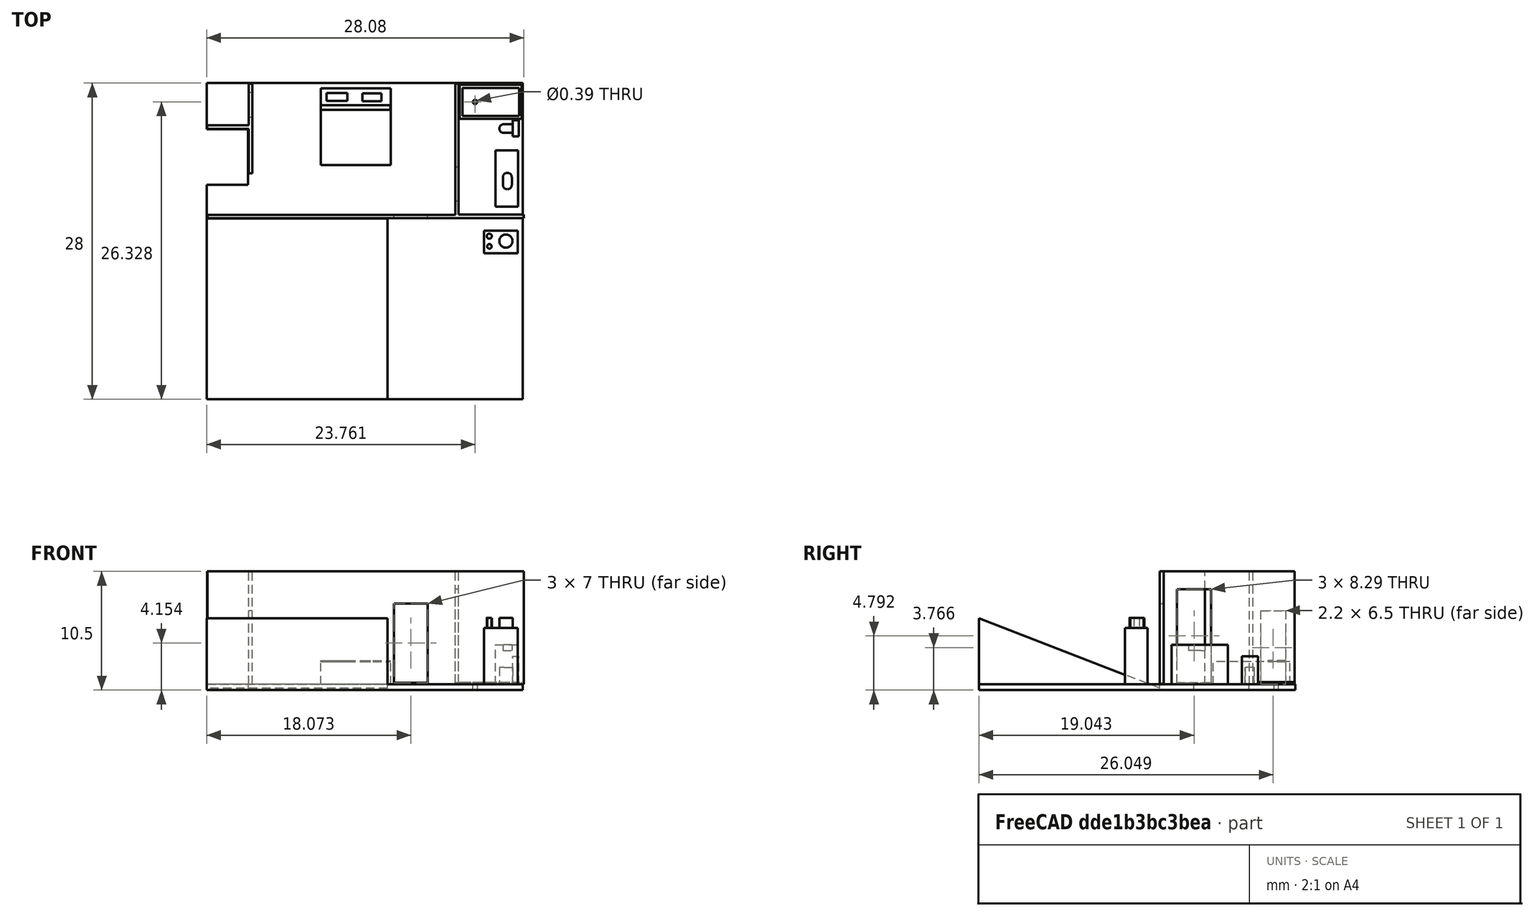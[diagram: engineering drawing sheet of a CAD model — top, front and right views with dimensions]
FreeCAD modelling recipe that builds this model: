
FCSTD DOCUMENT  (FreeCAD 0.19R)
Label: Addtion2ndStoryC
License: All rights reserved
LicenseURL: http://en.wikipedia.org/wiki/All_rights_reserved
objects: Sketcher::SketchObject×18, PartDesign::Pad×11, PartDesign::Pocket×7, PartDesign::Body×1, Mesh::Feature×1
note: 55 computed .brp shape members not serialized (recipe doc carries the construction recipe); baked Part::Feature solids carry a one-line shape summary decoded from their .brp

FEATURE [Sketcher::SketchObject] Sketch
  FullyConstrained = true
  MapMode = 5
  Support = -> [XY_Plane]
  sketch-geometry (6):
    g0: LineSegment StartX=-16 StartY=12 StartZ=0 EndX=12 EndY=12 EndZ=0
    g1: LineSegment StartX=0 StartY=0 StartZ=0 EndX=-16 EndY=0 EndZ=0
    g2: LineSegment StartX=-16 StartY=0 StartZ=0 EndX=-16 EndY=12 EndZ=0
    g3: LineSegment StartX=12 StartY=12 StartZ=0 EndX=12 EndY=-16 EndZ=0
    g4: LineSegment StartX=12 StartY=-16 StartZ=0 EndX=0 EndY=-16 EndZ=0
    g5: LineSegment StartX=0 StartY=-16 StartZ=0 EndX=0 EndY=0 EndZ=0
  constraints (17):
    c: Coincident(g1,g2)
    c: Coincident(g2,g0)
    c: Horizontal(g0)
    c: Horizontal(g1)
    c: Vertical(g2)
    c: DistanceX(g0) = 12
    c: DistanceX(g0) = -16
    c: DistanceY(g0) = 12
    c: Coincident(g1,g-1)
    c: Coincident(g0,g3)
    c: Coincident(g3,g4)
    c: PointOnObject(g4,g-2)
    c: Coincident(g4,g5)
    c: Coincident(g5,g1)
    c: Vertical(g3)
    c: Horizontal(g4)
    c: Distance(g5) = 16
FEATURE [PartDesign::Pad] Pad
  Direction = (1,1,1)
  Length = 0.5
  Length2 = 100
  Profile = -> Sketch
  Type = 0
FEATURE [Sketcher::SketchObject] Sketch001
  FullyConstrained = false
  MapMode = 5
  Placement = pos=(0,0,0.5) rot=(0,0,1;0rad)
  Support = -> [Pad]
  sketch-geometry (17):
    g0: LineSegment StartX=-15.9532 StartY=7.94663 StartZ=0 EndX=-15.9532 EndY=8.27663 EndZ=0
    g1: LineSegment StartX=-12.2832 StartY=11.9466 StartZ=0 EndX=-11.9532 EndY=11.9466 EndZ=0
    g2: LineSegment StartX=-11.9532 StartY=11.9466 StartZ=0 EndX=-11.9532 EndY=7.94663 EndZ=0
    g3: LineSegment StartX=12.0789 StartY=0.353614 StartZ=0 EndX=12.0789 EndY=0.023614 EndZ=0
    g4: LineSegment StartX=12.0789 StartY=0.023614 StartZ=0 EndX=-15.9253 EndY=0.023614 EndZ=0
    g5: LineSegment StartX=-15.9253 StartY=0.023614 StartZ=0 EndX=-15.9253 EndY=0.33 EndZ=0
    g6: LineSegment StartX=6.3 StartY=11.9503 StartZ=0 EndX=6 EndY=11.9503 EndZ=0
    g7: LineSegment StartX=6 StartY=11.9503 StartZ=0 EndX=6 EndY=0.33 EndZ=0
    g8: LineSegment StartX=6.3 StartY=0.353614 StartZ=0 EndX=6.3 EndY=11.9503 EndZ=0
    g9: LineSegment StartX=-15.9253 StartY=0.33 StartZ=0 EndX=6 EndY=0.33 EndZ=0
    g10: LineSegment StartX=6.3 StartY=0.353614 StartZ=0 EndX=12.0789 EndY=0.353614 EndZ=0
    g11: LineSegment StartX=-15.9532 StartY=8.27663 StartZ=0 EndX=-12.2832 EndY=8.27663 EndZ=0
    g12: LineSegment StartX=-12.2832 StartY=11.9466 StartZ=0 EndX=-12.2832 EndY=8.27663 EndZ=0
    g13: LineSegment StartX=-15.9532 StartY=7.94663 StartZ=0 EndX=-12.2832 EndY=7.94663 EndZ=0
    g14: LineSegment StartX=-12.2832 StartY=7.94663 StartZ=0 EndX=-12.2832 EndY=4 EndZ=0
    g15: LineSegment StartX=-12.2832 StartY=4 StartZ=0 EndX=-11.9532 EndY=4 EndZ=0
    g16: LineSegment StartX=-11.9532 StartY=7.94663 StartZ=0 EndX=-11.9532 EndY=4 EndZ=0
  constraints (40):
    c: Vertical(g0)
    c: Coincident(g1,g2)
    c: Horizontal(g1)
    c: Vertical(g2)
    c: Distance(g1) = 0.33
    c: Distance(g0) = 0.33
    c: Distance(g2) = 4
    c: Coincident(g3,g4)
    c: Coincident(g4,g5)
    c: Horizontal(g4)
    c: Vertical(g3)
    c: Vertical(g5)
    c: Distance(g3) = 0.33
    c: Coincident(g6,g7)
    c: Coincident(g8,g6)
    c: Horizontal(g6)
    c: Vertical(g7)
    c: Vertical(g8)
    c: Distance(g6) = 0.3
    c: DistanceX(g6) = 6
    c: Coincident(g9,g5)
    c: Coincident(g9,g7)
    c: Horizontal(g9)
    c: Coincident(g10,g8)
    c: Coincident(g10,g3)
    c: Horizontal(g10)
    c: Coincident(g11,g0)
    c: Horizontal(g11)
    c: Coincident(g12,g1)
    c: Coincident(g12,g11)
    c: Vertical(g12)
    c: Coincident(g13,g0)
    c: Horizontal(g13)
    c: Vertical(g14)
    c: Coincident(g15,g14)
    c: Coincident(g16,g15)
    c: Vertical(g16)
    c: DistanceY(g15) = 4
    c: Horizontal(g15)
    c: DistanceY(g7) = 0.33
FEATURE [PartDesign::Pad] Pad001
  BaseFeature = -> Pad
  Direction = (1,1,1)
  Length = 10
  Length2 = 100
  Profile = -> Sketch001
  Type = 0
FEATURE [Sketcher::SketchObject] Sketch002
  FullyConstrained = false
  MapMode = 5
  Placement = pos=(0,0,0.5) rot=(0,0,1;0rad)
  Support = -> [Pad001]
  sketch-geometry (4):
    g0: LineSegment StartX=-16.4037 StartY=7.90912 StartZ=0 EndX=-12.3288 EndY=7.90912 EndZ=0
    g1: LineSegment StartX=-12.3288 StartY=7.90912 StartZ=0 EndX=-12.3288 EndY=3 EndZ=0
    g2: LineSegment StartX=-12.3288 StartY=3 StartZ=0 EndX=-16.4037 EndY=3 EndZ=0
    g3: LineSegment StartX=-16.4037 StartY=3 StartZ=0 EndX=-16.4037 EndY=7.90912 EndZ=0
  constraints (9):
    c: Coincident(g0,g1)
    c: Coincident(g1,g2)
    c: Coincident(g2,g3)
    c: Coincident(g3,g0)
    c: Horizontal(g0)
    c: Horizontal(g2)
    c: Vertical(g1)
    c: Vertical(g3)
    c: DistanceY(g1) = 3
FEATURE [PartDesign::Pocket] Pocket
  BaseFeature = -> Pad001
  Length = 5
  Length2 = 100
  Profile = -> Sketch002
  Type = 0
FEATURE [Sketcher::SketchObject] Sketch003
  FullyConstrained = false
  MapMode = 5
  Placement = pos=(6.3,0,0) rot=(0.57735,0.57735,0.57735;2.0944rad)
  Support = -> [Pocket]
  sketch-geometry (4):
    g0: LineSegment StartX=1.54342 StartY=8.93566 StartZ=0 EndX=4.54342 EndY=8.93566 EndZ=0
    g1: LineSegment StartX=4.54342 StartY=8.93566 StartZ=0 EndX=4.54342 EndY=0.648454 EndZ=0
    g2: LineSegment StartX=4.54342 StartY=0.648454 StartZ=0 EndX=1.54342 EndY=0.648454 EndZ=0
    g3: LineSegment StartX=1.54342 StartY=0.648454 StartZ=0 EndX=1.54342 EndY=8.93566 EndZ=0
  constraints (9):
    c: Coincident(g0,g1)
    c: Coincident(g1,g2)
    c: Coincident(g2,g3)
    c: Coincident(g3,g0)
    c: Horizontal(g0)
    c: Horizontal(g2)
    c: Vertical(g1)
    c: Vertical(g3)
    c: Distance(g0) = 3
FEATURE [PartDesign::Pocket] Pocket001
  BaseFeature = -> Pocket
  Length = 5
  Length2 = 100
  Profile = -> Sketch003
  Type = 0
FEATURE [Sketcher::SketchObject] Sketch004
  FullyConstrained = false
  MapMode = 5
  Placement = pos=(0,0.023614,0) rot=(1,0,0;1.5708rad)
  Support = -> [Pocket001]
  sketch-geometry (4):
    g0: LineSegment StartX=0.573152 StartY=7.65396 StartZ=0 EndX=3.57315 EndY=7.65396 EndZ=0
    g1: LineSegment StartX=3.57315 StartY=7.65396 StartZ=0 EndX=3.57315 EndY=0.653959 EndZ=0
    g2: LineSegment StartX=3.57315 StartY=0.653959 StartZ=0 EndX=0.573152 EndY=0.653959 EndZ=0
    g3: LineSegment StartX=0.573152 StartY=0.653959 StartZ=0 EndX=0.573152 EndY=7.65396 EndZ=0
  constraints (10):
    c: Coincident(g0,g1)
    c: Coincident(g1,g2)
    c: Coincident(g2,g3)
    c: Coincident(g3,g0)
    c: Horizontal(g0)
    c: Horizontal(g2)
    c: Vertical(g1)
    c: Vertical(g3)
    c: Distance(g0) = 3
    c: Distance(g1) = 7
FEATURE [PartDesign::Pocket] Pocket002
  BaseFeature = -> Pocket001
  Length = 5
  Length2 = 100
  Profile = -> Sketch004
  Type = 0
FEATURE [Sketcher::SketchObject] Sketch005
  FullyConstrained = false
  MapMode = 5
  Placement = pos=(-11.9532,0,0) rot=(0.57735,0.57735,0.57735;2.0944rad)
  Support = -> [Pocket002]
  sketch-geometry (4):
    g0: LineSegment StartX=8.94938 StartY=7.01579 StartZ=0 EndX=11.1494 EndY=7.01579 EndZ=0
    g1: LineSegment StartX=11.1494 StartY=7.01579 StartZ=0 EndX=11.1494 EndY=0.51579 EndZ=0
    g2: LineSegment StartX=11.1494 StartY=0.51579 StartZ=0 EndX=8.94938 EndY=0.51579 EndZ=0
    g3: LineSegment StartX=8.94938 StartY=0.51579 StartZ=0 EndX=8.94938 EndY=7.01579 EndZ=0
  constraints (10):
    c: Coincident(g0,g1)
    c: Coincident(g1,g2)
    c: Coincident(g2,g3)
    c: Coincident(g3,g0)
    c: Horizontal(g0)
    c: Horizontal(g2)
    c: Vertical(g1)
    c: Vertical(g3)
    c: Distance(g0) = 2.2
    c: Distance(g1) = 6.5
FEATURE [PartDesign::Pocket] Pocket003
  BaseFeature = -> Pocket002
  Length = 5
  Length2 = 100
  Profile = -> Sketch005
  Type = 0
FEATURE [Sketcher::SketchObject] Sketch006
  FullyConstrained = false
  MapMode = 5
  Placement = pos=(0,0,0.5) rot=(0,0,1;0rad)
  Support = -> [Pocket003]
  sketch-geometry (4):
    g0: LineSegment StartX=6.38983 StartY=11.8429 StartZ=0 EndX=11.8898 EndY=11.8429 EndZ=0
    g1: LineSegment StartX=11.8898 StartY=11.8429 StartZ=0 EndX=11.8898 EndY=8.84289 EndZ=0
    g2: LineSegment StartX=11.8898 StartY=8.84289 StartZ=0 EndX=6.38983 EndY=8.84289 EndZ=0
    g3: LineSegment StartX=6.38983 StartY=8.84289 StartZ=0 EndX=6.38983 EndY=11.8429 EndZ=0
  constraints (10):
    c: Coincident(g0,g1)
    c: Coincident(g1,g2)
    c: Coincident(g2,g3)
    c: Coincident(g3,g0)
    c: Horizontal(g0)
    c: Horizontal(g2)
    c: Vertical(g1)
    c: Vertical(g3)
    c: Distance(g2) = 5.5
    c: Distance(g1) = 3
FEATURE [PartDesign::Pad] Pad002
  BaseFeature = -> Pocket003
  Direction = (1,1,1)
  Length = 0.2
  Length2 = 100
  Profile = -> Sketch006
  Type = 0
FEATURE [Sketcher::SketchObject] Sketch007
  FullyConstrained = false
  MapMode = 5
  Placement = pos=(0,0,0.7) rot=(0,0,1;0rad)
  Support = -> [Pad002]
  sketch-geometry (4):
    g0: LineSegment StartX=6.64692 StartY=11.5659 StartZ=0 EndX=11.6693 EndY=11.5659 EndZ=0
    g1: LineSegment StartX=11.6693 StartY=11.5659 StartZ=0 EndX=11.6693 EndY=9.09872 EndZ=0
    g2: LineSegment StartX=11.6693 StartY=9.09872 StartZ=0 EndX=6.64692 EndY=9.09872 EndZ=0
    g3: LineSegment StartX=6.64692 StartY=9.09872 StartZ=0 EndX=6.64692 EndY=11.5659 EndZ=0
  constraints (8):
    c: Coincident(g0,g1)
    c: Coincident(g1,g2)
    c: Coincident(g2,g3)
    c: Coincident(g3,g0)
    c: Horizontal(g0)
    c: Horizontal(g2)
    c: Vertical(g1)
    c: Vertical(g3)
FEATURE [PartDesign::Pocket] Pocket004
  BaseFeature = -> Pad002
  Length = 0.2
  Length2 = 100
  Profile = -> Sketch007
  Type = 0
FEATURE [Sketcher::SketchObject] Sketch008
  FullyConstrained = false
  MapMode = 5
  Placement = pos=(0,0,0.5) rot=(0,0,1;0rad)
  Support = -> [Pocket004]
  sketch-geometry (4):
    g0: ArcOfCircle CenterX=10.2998 CenterY=7.96616 CenterZ=0 NormalX=0 NormalY=0 NormalZ=1 AngleXU=0 Radius=0.384687 StartAngle=1.5708 EndAngle=4.71239
    g1: ArcOfCircle CenterX=11.0789 CenterY=7.96616 CenterZ=0 NormalX=0 NormalY=0 NormalZ=1 AngleXU=0 Radius=0.384687 StartAngle=4.71239 EndAngle=7.85398
    g2: LineSegment StartX=10.2998 StartY=7.58147 StartZ=0 EndX=11.0789 EndY=7.58147 EndZ=0
    g3: LineSegment StartX=10.2998 StartY=8.35084 StartZ=0 EndX=11.0789 EndY=8.35084 EndZ=0
  constraints (6):
    c: Tangent(g0,g3) = 1.5708
    c: Tangent(g0,g2) = -1.5708
    c: Tangent(g2,g1) = -1.5708
    c: Tangent(g3,g1) = 1.5708
    c: Horizontal(g2)
    c: Equal(g0,g1)
FEATURE [PartDesign::Pad] Pad003
  BaseFeature = -> Pocket004
  Direction = (1,1,1)
  Length = 1.5
  Length2 = 100
  Profile = -> Sketch008
  Type = 0
FEATURE [Sketcher::SketchObject] Sketch009
  FullyConstrained = false
  MapMode = 5
  Placement = pos=(0,0,0.5) rot=(0,0,1;0rad)
  Support = -> [Pad003]
  sketch-geometry (4):
    g0: LineSegment StartX=11.1017 StartY=8.69932 StartZ=0 EndX=11.648 EndY=8.69932 EndZ=0
    g1: LineSegment StartX=11.648 StartY=8.69932 StartZ=0 EndX=11.648 EndY=7.2719 EndZ=0
    g2: LineSegment StartX=11.648 StartY=7.2719 StartZ=0 EndX=11.1017 EndY=7.2719 EndZ=0
    g3: LineSegment StartX=11.1017 StartY=7.2719 StartZ=0 EndX=11.1017 EndY=8.69932 EndZ=0
  constraints (8):
    c: Coincident(g0,g1)
    c: Coincident(g1,g2)
    c: Coincident(g2,g3)
    c: Coincident(g3,g0)
    c: Horizontal(g0)
    c: Horizontal(g2)
    c: Vertical(g1)
    c: Vertical(g3)
FEATURE [PartDesign::Pad] Pad004
  BaseFeature = -> Pad003
  Direction = (1,1,1)
  Length = 2.5
  Length2 = 100
  Profile = -> Sketch009
  Type = 0
FEATURE [Sketcher::SketchObject] Sketch010
  FullyConstrained = false
  MapMode = 5
  Placement = pos=(0,0,0.5) rot=(0,0,1;0rad)
  Support = -> [Pad004]
  sketch-geometry (4):
    g0: LineSegment StartX=9.57943 StartY=6.04354 StartZ=0 EndX=11.5794 EndY=6.04354 EndZ=0
    g1: LineSegment StartX=11.5794 StartY=6.04354 StartZ=0 EndX=11.5794 EndY=1.04354 EndZ=0
    g2: LineSegment StartX=11.5794 StartY=1.04354 StartZ=0 EndX=9.57943 EndY=1.04354 EndZ=0
    g3: LineSegment StartX=9.57943 StartY=1.04354 StartZ=0 EndX=9.57943 EndY=6.04354 EndZ=0
  constraints (10):
    c: Coincident(g0,g1)
    c: Coincident(g1,g2)
    c: Coincident(g2,g3)
    c: Coincident(g3,g0)
    c: Horizontal(g0)
    c: Horizontal(g2)
    c: Vertical(g1)
    c: Vertical(g3)
    c: Distance(g3) = 5
    c: Distance(g0) = 2
FEATURE [PartDesign::Pad] Pad005
  BaseFeature = -> Pad004
  Direction = (1,1,1)
  Length = 3.5
  Length2 = 100
  Profile = -> Sketch010
  Type = 0
FEATURE [Sketcher::SketchObject] Sketch011
  FullyConstrained = false
  MapMode = 5
  Placement = pos=(0,0,4) rot=(0,0,1;0rad)
  Support = -> [Pad005]
  sketch-geometry (4):
    g0: ArcOfCircle CenterX=10.6211 CenterY=3.65295 CenterZ=0 NormalX=0 NormalY=0 NormalZ=1 AngleXU=0 Radius=0.396821 StartAngle=4e-16 EndAngle=3.14159
    g1: ArcOfCircle CenterX=10.6211 CenterY=2.98754 CenterZ=0 NormalX=0 NormalY=0 NormalZ=1 AngleXU=0 Radius=0.396821 StartAngle=3.14159 EndAngle=6.28319
    g2: LineSegment StartX=10.2243 StartY=3.65295 StartZ=0 EndX=10.2243 EndY=2.98754 EndZ=0
    g3: LineSegment StartX=11.0179 StartY=3.65295 StartZ=0 EndX=11.0179 EndY=2.98754 EndZ=0
  constraints (6):
    c: Tangent(g0,g3) = 1.5708
    c: Tangent(g0,g2) = -1.5708
    c: Tangent(g2,g1) = -1.5708
    c: Tangent(g3,g1) = 1.5708
    c: Vertical(g2)
    c: Equal(g0,g1)
FEATURE [PartDesign::Pocket] Pocket005
  BaseFeature = -> Pad005
  Length = 0.5
  Length2 = 100
  Profile = -> Sketch011
  Type = 0
FEATURE [Sketcher::SketchObject] Sketch012
  FullyConstrained = false
  MapMode = 5
  Placement = pos=(0,0,0.5) rot=(0,0,1;0rad)
  Support = -> [Pocket005]
  sketch-geometry (4):
    g0: LineSegment StartX=8.54799 StartY=-1.06451 StartZ=0 EndX=11.548 EndY=-1.06451 EndZ=0
    g1: LineSegment StartX=11.548 StartY=-1.06451 StartZ=0 EndX=11.548 EndY=-3.06451 EndZ=0
    g2: LineSegment StartX=11.548 StartY=-3.06451 StartZ=0 EndX=8.54799 EndY=-3.06451 EndZ=0
    g3: LineSegment StartX=8.54799 StartY=-3.06451 StartZ=0 EndX=8.54799 EndY=-1.06451 EndZ=0
  constraints (10):
    c: Coincident(g0,g1)
    c: Coincident(g1,g2)
    c: Coincident(g2,g3)
    c: Coincident(g3,g0)
    c: Horizontal(g0)
    c: Horizontal(g2)
    c: Vertical(g1)
    c: Vertical(g3)
    c: Distance(g0) = 3
    c: Distance(g3) = 2
FEATURE [PartDesign::Pad] Pad006
  BaseFeature = -> Pocket005
  Direction = (1,1,1)
  Length = 5
  Length2 = 100
  Profile = -> Sketch012
  Type = 0
FEATURE [Sketcher::SketchObject] Sketch013
  FullyConstrained = false
  MapMode = 5
  Placement = pos=(0,0,5.5) rot=(0,0,1;0rad)
  Support = -> [Pad006]
  sketch-geometry (3):
    g0: Circle CenterX=10.4922 CenterY=-1.99827 CenterZ=0 NormalX=0 NormalY=0 NormalZ=1 AngleXU=0 Radius=0.586594
    g1: Circle CenterX=9.02211 CenterY=-1.56306 CenterZ=0 NormalX=0 NormalY=0 NormalZ=1 AngleXU=0 Radius=0.221942
    g2: Circle CenterX=9.03178 CenterY=-2.46251 CenterZ=0 NormalX=0 NormalY=0 NormalZ=1 AngleXU=0 Radius=0.200927
FEATURE [PartDesign::Pad] Pad007
  BaseFeature = -> Pad006
  Direction = (1,1,1)
  Length = 0.9
  Length2 = 100
  Profile = -> Sketch013
  Type = 0
FEATURE [Sketcher::SketchObject] Sketch014
  FullyConstrained = false
  MapMode = 5
  Placement = pos=(0,0,0) rot=(0.57735,-0.57735,-0.57735;2.0944rad)
  Support = -> [Pad007]
  sketch-geometry (3):
    g0: LineSegment StartX=-0.434067 StartY=0 StartZ=0 EndX=16 EndY=6.36 EndZ=0
    g1: LineSegment StartX=16 StartY=6.36 StartZ=0 EndX=16 EndY=0 EndZ=0
    g2: LineSegment StartX=16 StartY=0 StartZ=0 EndX=-0.434067 EndY=0 EndZ=0
  constraints (8):
    c: PointOnObject(g0,g-1)
    c: Coincident(g0,g1)
    c: PointOnObject(g1,g-1)
    c: Vertical(g1)
    c: Coincident(g1,g2)
    c: Coincident(g2,g0)
    c: DistanceX(g1) = 16
    c: DistanceY(g1,g1) = 6.36
FEATURE [PartDesign::Pad] Pad008
  BaseFeature = -> Pad007
  Direction = (1,1,1)
  Length = 16
  Length2 = 100
  Profile = -> Sketch014
  Type = 0
FEATURE [Sketcher::SketchObject] Sketch015
  FullyConstrained = false
  MapMode = 5
  Placement = pos=(0,0,0.5) rot=(0,0,1;0rad)
  Support = -> [Pad008]
  sketch-geometry (4):
    g0: LineSegment StartX=-5.89716 StartY=11.5438 StartZ=0 EndX=0.302838 EndY=11.5438 EndZ=0
    g1: LineSegment StartX=0.302838 StartY=11.5438 StartZ=0 EndX=0.302838 EndY=4.74384 EndZ=0
    g2: LineSegment StartX=0.302838 StartY=4.74384 StartZ=0 EndX=-5.89716 EndY=4.74384 EndZ=0
    g3: LineSegment StartX=-5.89716 StartY=4.74384 StartZ=0 EndX=-5.89716 EndY=11.5438 EndZ=0
  constraints (10):
    c: Coincident(g0,g1)
    c: Coincident(g1,g2)
    c: Coincident(g2,g3)
    c: Coincident(g3,g0)
    c: Horizontal(g0)
    c: Horizontal(g2)
    c: Vertical(g1)
    c: Vertical(g3)
    c: Distance(g3) = 6.8
    c: Distance(g0) = 6.2
FEATURE [PartDesign::Pad] Pad009
  BaseFeature = -> Pad008
  Direction = (1,1,1)
  Length = 2
  Length2 = 100
  Profile = -> Sketch015
  Type = 0
FEATURE [Sketcher::SketchObject] Sketch016
  FullyConstrained = false
  MapMode = 5
  Placement = pos=(0,0,2.5) rot=(0,0,1;0rad)
  Support = -> [Pad009]
  sketch-geometry (12):
    g0: LineSegment StartX=-5.87675 StartY=10.0323 StartZ=0 EndX=0.275035 EndY=10.0323 EndZ=0
    g1: LineSegment StartX=0.275035 StartY=10.0323 StartZ=0 EndX=0.275035 EndY=9.61171 EndZ=0
    g2: LineSegment StartX=0.275035 StartY=9.61171 StartZ=0 EndX=-5.87675 EndY=9.61171 EndZ=0
    g3: LineSegment StartX=-5.87675 StartY=9.61171 StartZ=0 EndX=-5.87675 EndY=10.0323 EndZ=0
    g4: LineSegment StartX=-5.37428 StartY=11.1323 StartZ=0 EndX=-3.54154 EndY=11.1323 EndZ=0
    g5: LineSegment StartX=-3.54154 StartY=11.1323 StartZ=0 EndX=-3.54154 EndY=10.4274 EndZ=0
    g6: LineSegment StartX=-3.54154 StartY=10.4274 StartZ=0 EndX=-5.37428 EndY=10.4274 EndZ=0
    g7: LineSegment StartX=-5.37428 StartY=10.4274 StartZ=0 EndX=-5.37428 EndY=11.1323 EndZ=0
    g8: LineSegment StartX=-2.21985 StartY=11.0971 StartZ=0 EndX=-0.510471 EndY=11.0971 EndZ=0
    g9: LineSegment StartX=-0.510471 StartY=11.0971 StartZ=0 EndX=-0.510471 EndY=10.3922 EndZ=0
    g10: LineSegment StartX=-0.510471 StartY=10.3922 StartZ=0 EndX=-2.21985 EndY=10.3922 EndZ=0
    g11: LineSegment StartX=-2.21985 StartY=10.3922 StartZ=0 EndX=-2.21985 EndY=11.0971 EndZ=0
  constraints (24):
    c: Coincident(g0,g1)
    c: Coincident(g1,g2)
    c: Coincident(g2,g3)
    c: Coincident(g3,g0)
    c: Horizontal(g0)
    c: Horizontal(g2)
    c: Vertical(g1)
    c: Vertical(g3)
    c: Coincident(g4,g5)
    c: Coincident(g5,g6)
    c: Coincident(g6,g7)
    c: Coincident(g7,g4)
    c: Horizontal(g4)
    c: Horizontal(g6)
    c: Vertical(g5)
    c: Vertical(g7)
    c: Coincident(g8,g9)
    c: Coincident(g9,g10)
    c: Coincident(g10,g11)
    c: Coincident(g11,g8)
    c: Horizontal(g8)
    c: Horizontal(g10)
    c: Vertical(g9)
    c: Vertical(g11)
FEATURE [PartDesign::Pad] Pad010
  BaseFeature = -> Pad009
  Direction = (1,1,1)
  Length = 0.1
  Length2 = 100
  Profile = -> Sketch016
  Type = 0
FEATURE [Sketcher::SketchObject] Sketch017
  FullyConstrained = false
  MapMode = 5
  Placement = pos=(0,0,0.5) rot=(0,0,1;0rad)
  Support = -> [Pad010]
  sketch-geometry (1):
    g0: Circle CenterX=7.76091 CenterY=10.3276 CenterZ=0 NormalX=0 NormalY=0 NormalZ=1 AngleXU=0 Radius=0.192706
FEATURE [PartDesign::Pocket] Pocket006
  BaseFeature = -> Pad010
  Length = 5
  Length2 = 100
  Profile = -> Sketch017
  Type = 0
FEATURE [PartDesign::Body] Body
  Group = -> [Sketch,Pad,Sketch001,Pad001,Sketch002,Pocket,Sketch003,Pocket001,Sketch004,Pocket002,Sketch005,Pocket003,Sketch006,Pad002,Sketch007,Pocket004,Sketch008,Pad003,Sketch009,Pad004,Sketch010,Pad005,Sketch011,Pocket005,Sketch012,Pad006,Sketch013,Pad007,Sketch014,Pad008,Sketch015,Pad009,Sketch016,Pad010,Sketch017,Pocket006]
  Origin = -> Origin
  Tip = -> Pocket006
FEATURE [Mesh::Feature] Mesh  label="Pocket006 (Meshed)"
